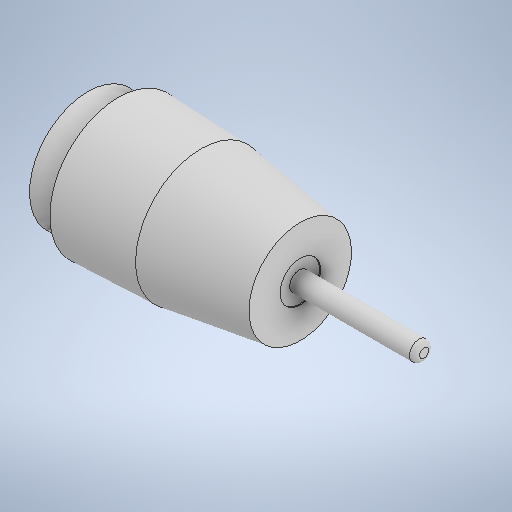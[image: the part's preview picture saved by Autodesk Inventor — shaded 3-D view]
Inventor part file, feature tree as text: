
AUTODESK INVENTOR PART (.ipt)
format: ipt  version: 2025 (Build 290162000, 162)  size: 267,264 bytes
history: native  units: in
note: dims shown in document units (in); Inventor stores cm internally (conversion verified against a paired STEP export)
features: sketch x3, extrude x2, revolve x1
ambient origin geometry x8: Origin, YZ Plane, XZ Plane, XY Plane, X Axis, Y Axis, Z Axis, Center Point
bodies: Solid1 (feature_tree)
feature tree (6):
  revolve  "Revolution1"  [1 undecoded]
  extrude  "Extrusion1"  Depth=0.7087in
  extrude  "Extrusion2"  Depth=0.0197in
  sketch  "Sketch1"  dims[d0=0.2264in d1=0.1181in]
  sketch  "Sketch2"  dims[d2=0.0394in d3=0.7087in]
  sketch  "Sketch3"  dims[d5=0.4803in d6=0.0197in d7=90.0deg d8=0.1575in d9=0.7874in d10=0.0in d11=0.0374in d12=0.1575in d13=0.0039in d14=0.0in]
note: 1 required parameter value undecoded (feature->parameter linkage not recoverable at this tier; creation-order binding heuristic only, values carry confidence <= 0.55)
